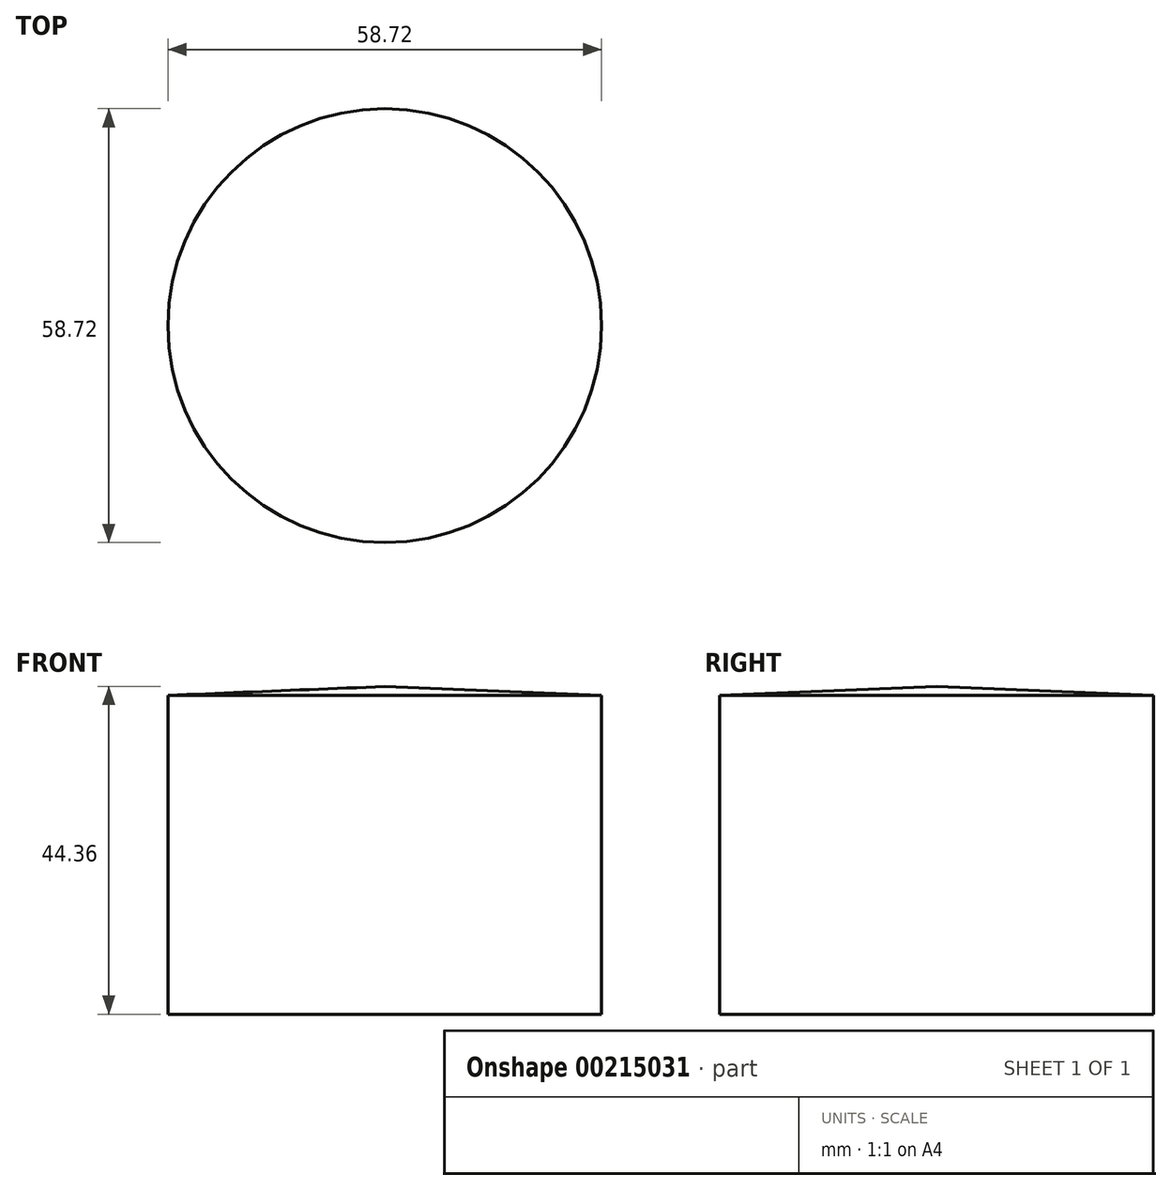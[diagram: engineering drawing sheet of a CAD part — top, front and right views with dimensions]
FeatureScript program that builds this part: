
annotation { "Feature Type Name" : "Feature", "Feature Type Description" : "" }
export const myFeature = defineFeature(function(context is Context, id is Id, definition is map)
    precondition{}
    {
        {
            var Q0;
            Q0=qCreatedBy(makeId("Front.planeOp"),FACE);
            var sketch = newSketch(context, id + "F0", { "sketchPlane" : qUnion([Q0])});
            skLineSegment(sketch, "E0", {"start": v(-29.36, 21.88) * mm, "end": v(-29.36, -21.27) * mm});
            skLineSegment(sketch, "E1", {"start": v(-29.36, -21.27) * mm, "end": v(0, -21.27) * mm});
            skLineSegment(sketch, "E2", {"start": v(0, -21.27) * mm, "end": v(0, 23.1) * mm});
            skLineSegment(sketch, "E3", {"start": v(0, 23.1) * mm, "end": v(-29.36, 21.88) * mm});
            skLineSegment(sketch, "E4", {"start": v(0, 37.68) * mm, "end": v(0, -47.4) * mm, "construction": true});
            skSolve(sketch);
        }
        {
            var Q0;
            Q0 = qSketchRegion(id + "F0", true);
            var Q1;
            Q1=sQuery(id+"F0.wireOp",EDGE,"E4");
            revolve(context, id + "F1", {"entities" : qUnion([Q0]), "axis" : qUnion([Q1]), "revolveType" : RevolveType.FULL});
        }
    });
